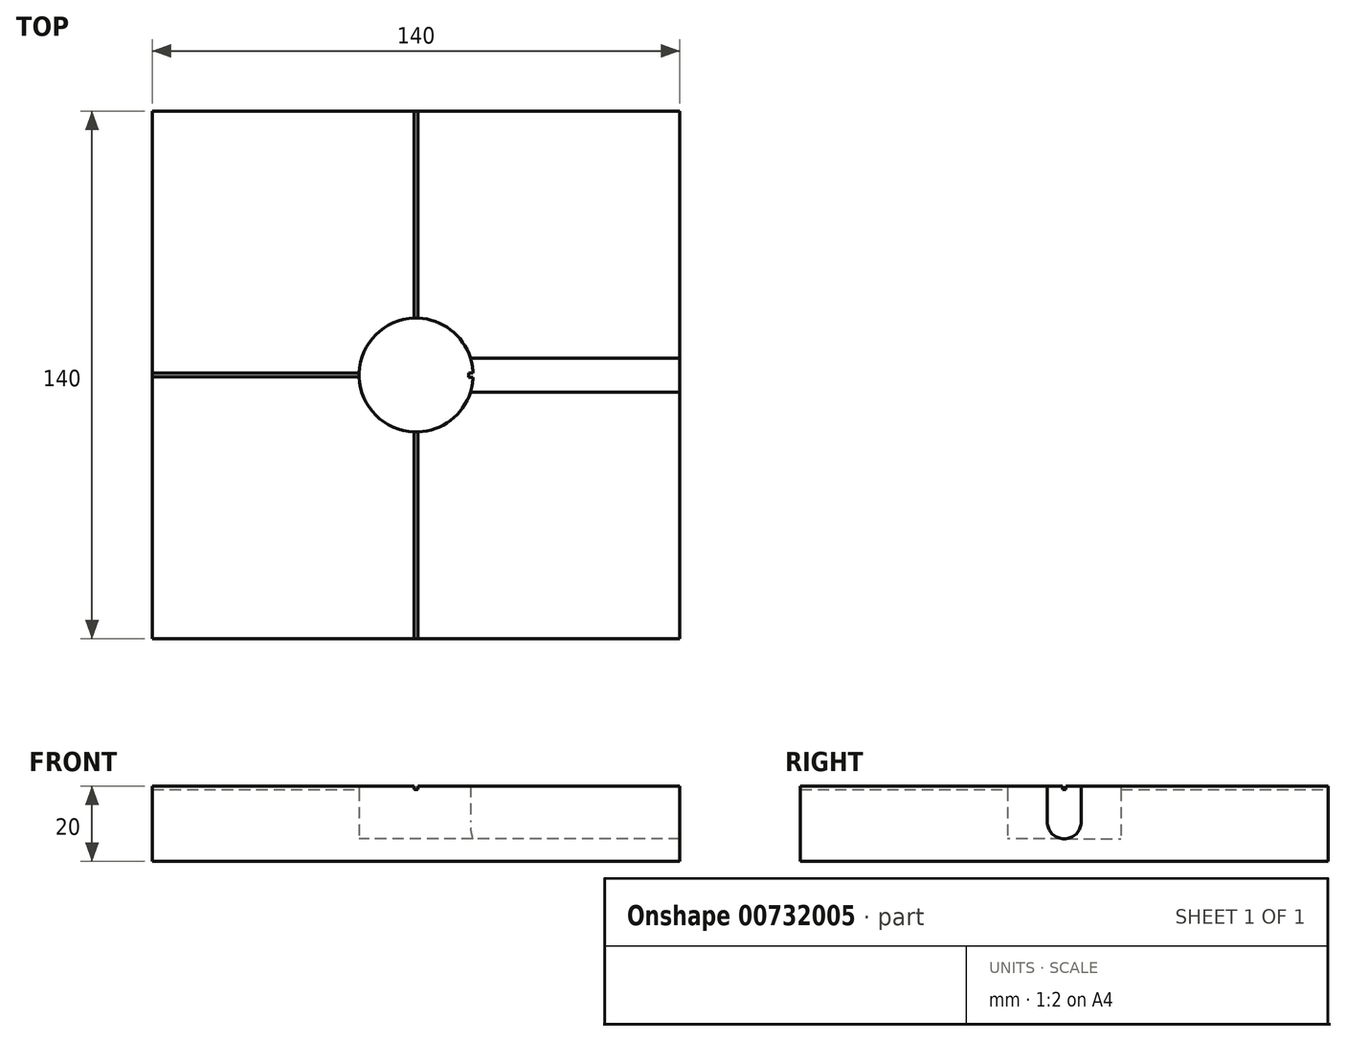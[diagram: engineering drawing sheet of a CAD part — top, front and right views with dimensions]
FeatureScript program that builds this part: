
annotation { "Feature Type Name" : "Feature", "Feature Type Description" : "" }
export const myFeature = defineFeature(function(context is Context, id is Id, definition is map)
    precondition{}
    {
        {
            var Q0;
            Q0=qCreatedBy(makeId("Front.planeOp"),FACE);
            var sketch = newSketch(context, id + "F0", { "sketchPlane" : qUnion([Q0])});
            skLineSegment(sketch, "E0", {"start": v(15.1, 20) * mm, "end": v(15.1, 6) * mm});
            skLineSegment(sketch, "E1", {"start": v(15.1, 6) * mm, "end": v(0, 6) * mm});
            skLineSegment(sketch, "E2", {"start": v(15.1, 20) * mm, "end": v(0, 20) * mm});
            skLineSegment(sketch, "E3", {"start": v(0, 20) * mm, "end": v(0, 6) * mm});
            skSolve(sketch);
        }
        {
            var Q0;
            Q0=qCreatedBy(makeId("Right.planeOp"),FACE);
            var sketch = newSketch(context, id + "F1", { "sketchPlane" : qUnion([Q0])});
            skLineSegment(sketch, "E4", {"start": v(0, 20.46) * mm, "end": v(-4.5, 20.46) * mm});
            skLineSegment(sketch, "E5", {"start": v(4.5, 20.46) * mm, "end": v(0, 20.46) * mm});
            skLineSegment(sketch, "E6", {"start": v(4.5, 20.46) * mm, "end": v(4.5, 10.46) * mm});
            skLineSegment(sketch, "E7", {"start": v(-4.5, 20.46) * mm, "end": v(-4.5, 10.46) * mm});
            skArc(sketch, "E8", {"start": v(4.5, 10.46) * mm, "mid": v(0, 5.96) * mm, "end": v(-4.5, 10.46) * mm});
            skSolve(sketch);
        }
        {
            var Q0;
            Q0=qCreatedBy(makeId("Top.planeOp"),FACE);
            var sketch = newSketch(context, id + "F2", { "sketchPlane" : qUnion([Q0])});
            skLineSegment(sketch, "E9", {"start": v(14, 0) * mm, "end": v(14, -0.5) * mm});
            skLineSegment(sketch, "E10", {"start": v(14, 0) * mm, "end": v(14, 0.5) * mm});
            skLineSegment(sketch, "E11", {"start": v(14, 0.5) * mm, "end": v(74, 0.5) * mm});
            skLineSegment(sketch, "E12", {"start": v(74, 0.5) * mm, "end": v(74, -0.5) * mm});
            skLineSegment(sketch, "E13", {"start": v(74, -0.5) * mm, "end": v(14, -0.5) * mm});
            skLineSegment(sketch, "E14", {"start": v(0, -14) * mm, "end": v(-0.5, -14) * mm});
            skLineSegment(sketch, "E15", {"start": v(0, -14) * mm, "end": v(0.5, -14) * mm});
            skLineSegment(sketch, "E16", {"start": v(0.5, -14) * mm, "end": v(0.5, -74) * mm});
            skLineSegment(sketch, "E17", {"start": v(0.5, -74) * mm, "end": v(-0.5, -74) * mm});
            skLineSegment(sketch, "E18", {"start": v(-0.5, -74) * mm, "end": v(-0.5, -14) * mm});
            skLineSegment(sketch, "E19", {"start": v(-14, 0) * mm, "end": v(-14, 0.5) * mm});
            skLineSegment(sketch, "E20", {"start": v(-14, 0) * mm, "end": v(-14, -0.5) * mm});
            skLineSegment(sketch, "E21", {"start": v(-14, -0.5) * mm, "end": v(-74, -0.5) * mm});
            skLineSegment(sketch, "E22", {"start": v(-74, -0.5) * mm, "end": v(-74, 0.5) * mm});
            skLineSegment(sketch, "E23", {"start": v(-74, 0.5) * mm, "end": v(-14, 0.5) * mm});
            skLineSegment(sketch, "E24", {"start": v(-0.5, 14) * mm, "end": v(-0.5, 74) * mm});
            skLineSegment(sketch, "E25", {"start": v(0.5, 74) * mm, "end": v(0.5, 14) * mm});
            skLineSegment(sketch, "E26", {"start": v(-0.5, 14) * mm, "end": v(0, 14) * mm});
            skLineSegment(sketch, "E27", {"start": v(0, 14) * mm, "end": v(0.5, 14) * mm});
            skLineSegment(sketch, "E28", {"start": v(-0.5, 74) * mm, "end": v(0.5, 74) * mm});
            skSolve(sketch);
        }
        {
            var Q0;
            Q0=qCreatedBy(makeId("Top.planeOp"),FACE);
            var sketch = newSketch(context, id + "F3", { "sketchPlane" : qUnion([Q0])});
            skLineSegment(sketch, "E29.bottom", {"start": v(-70, 70) * mm, "end": v(70, 70) * mm});
            skLineSegment(sketch, "E29.top", {"start": v(-70, -70) * mm, "end": v(70, -70) * mm});
            skLineSegment(sketch, "E29.left", {"start": v(-70, 70) * mm, "end": v(-70, -70) * mm});
            skLineSegment(sketch, "E29.right", {"start": v(70, 70) * mm, "end": v(70, -70) * mm});
            skSolve(sketch);
        }
        {
            var Q0;
            Q0=makeQuery(id+"F3.imprint","IMPRINT",FACE,{"disambiguationData":[TD([[makeQuery(id+"F3.imprint","IMPRINT",EDGE,{"derivedFrom":sQuery(id+"F3.wireOp",EDGE,"E29.bottom")}),-1.0]])]});
            extrude(context, id + "F4", {"entities" : qUnion([Q0]), "depth" : 20 * mm, "offsetDistance" : 25 * mm});
        }
        {
            var Q0;
            Q0=makeQuery(id+"F0.imprint","IMPRINT",FACE,{"disambiguationData":[TD([[makeQuery(id+"F0.imprint","IMPRINT",EDGE,{"derivedFrom":sQuery(id+"F0.wireOp",EDGE,"E0")}),-1.0]])]});
            var Q1;
            Q1=sQuery(id+"F0.wireOp",EDGE,"E3");
            revolve(context, id + "F5", {"operationType" : NewBodyOperationType.REMOVE, "surfaceOperationType" : NewSurfaceOperationType.NEW, "entities" : qUnion([Q0]), "axis" : qUnion([Q1]), "revolveType" : RevolveType.FULL, "oppositeDirection" : true});
        }
        {
            var Q0;
            Q0=makeQuery(id+"F1.imprint","IMPRINT",FACE,{"disambiguationData":[TD([[makeQuery(id+"F1.imprint","IMPRINT",EDGE,{"derivedFrom":sQuery(id+"F1.wireOp",EDGE,"E4")}),1.0]])]});
            extrude(context, id + "F6", {"entities" : qUnion([Q0]), "operationType" : NewBodyOperationType.REMOVE, "depth" : 150 * mm, "offsetDistance" : 25 * mm, "hasSecondDirection" : true, "secondDirectionOppositeDirection" : true, "secondDirectionDepth" : -14 * mm});
        }
        {
            var Q0;
            Q0 = qSketchRegion(id + "F2", true);
            extrude(context, id + "F7", {"entities" : qUnion([Q0]), "operationType" : NewBodyOperationType.REMOVE, "oppositeDirection" : true, "depth" : -25 * mm, "offsetDistance" : 25 * mm, "hasSecondDirection" : true, "secondDirectionOppositeDirection" : true, "secondDirectionDepth" : -19 * mm});
        }
    });
